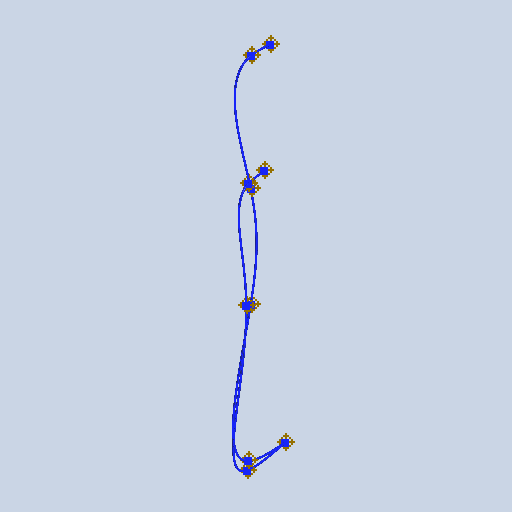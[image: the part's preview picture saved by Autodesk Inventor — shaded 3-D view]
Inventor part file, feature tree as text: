
AUTODESK INVENTOR PART (.ipt)
format: ipt  version: 2025 (Build 290162000, 162)  size: 237,056 bytes
history: native  units: mm (DEFAULTED — no unit token found)
features: other x14, plane x2, sketch x2, sweep x2
ambient origin geometry x8: Origin, YZ Plane, XZ Plane, XY Plane, X Axis, Y Axis, Z Axis, Center Point
bodies: Body1 (feature_tree), Body2 (feature_tree)
feature tree (20):
  other  "Work Point1"
  other  "Work Point2"
  other  "Segment1"
  other  "Work Point3"
  other  "Work Point4"
  other  "Work Point5"
  plane  "Work Plane1"
  other  "Work Point6"
  other  "Segment2"
  other  "Work Point7"
  other  "Work Point8"
  other  "Work Point9"
  other  "Work Point10"
  plane  "Work Plane2"
  sketch  "Sketch1"  dims[d0=0.0mm d1=0.0mm d2=0.0mm d3=0.0mm]
  other  "Srf1"
  sketch  "Sketch2"
  other  "Srf2"
  sweep  "SweepSrf1"
  sweep  "SweepSrf2"
